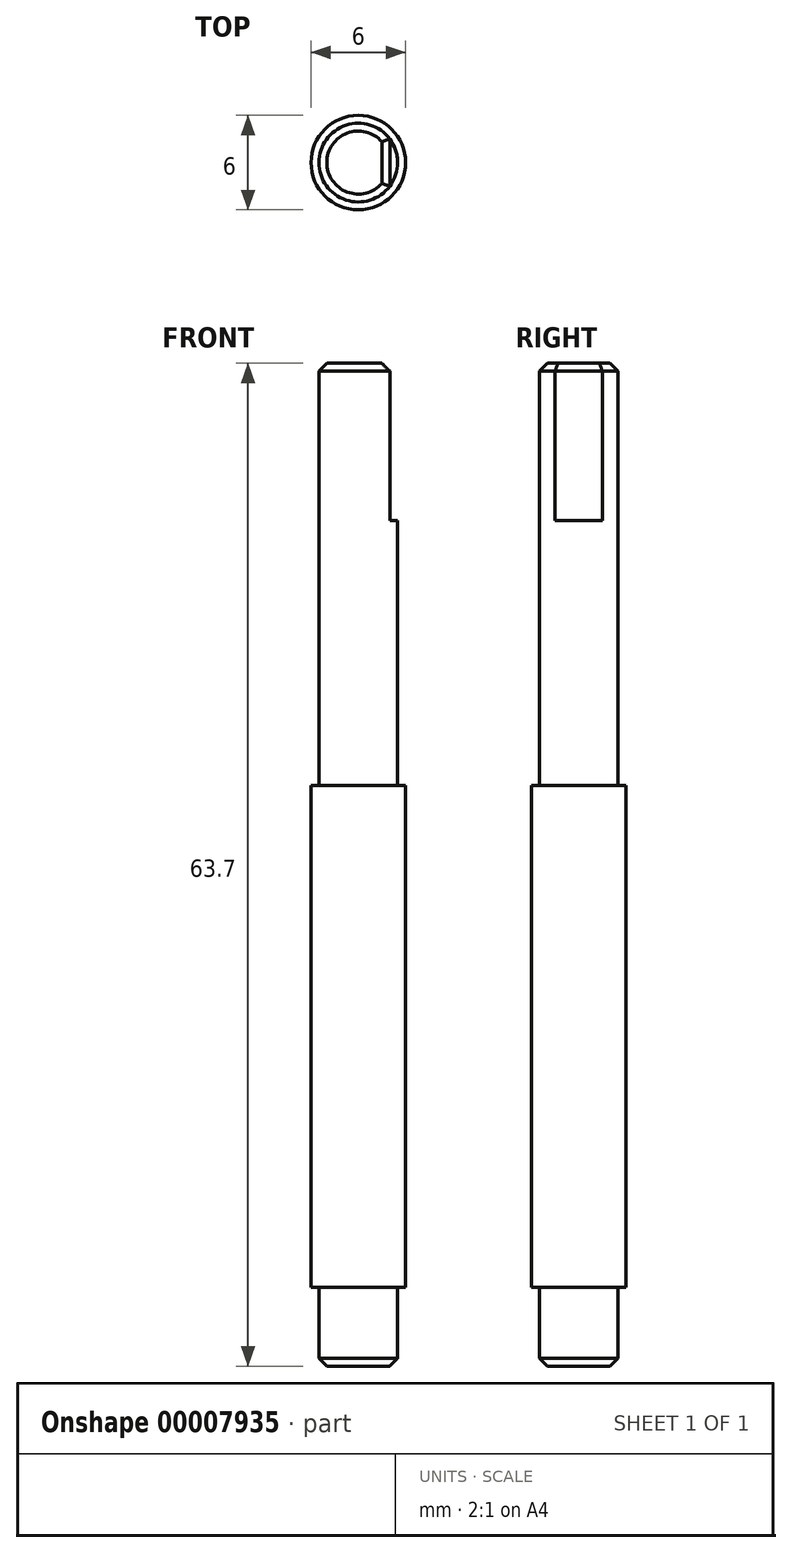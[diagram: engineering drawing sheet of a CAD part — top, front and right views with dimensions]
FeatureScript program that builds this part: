
annotation { "Feature Type Name" : "Feature", "Feature Type Description" : "" }
export const myFeature = defineFeature(function(context is Context, id is Id, definition is map)
    precondition{}
    {
        {
            var Q0;
            Q0=qCreatedBy(makeId("Top.planeOp"),FACE);
            var sketch = newSketch(context, id + "F0", { "sketchPlane" : qUnion([Q0])});
            skCircle(sketch, "E0", {"center": v(0, 0) * mm, "radius": 3 * mm});
            skCircle(sketch, "E1", {"center": v(0, 0) * mm, "radius": 2.5 * mm});
            skSolve(sketch);
        }
        {
            var Q0;
            Q0=makeQuery(id+"F0.imprint","IMPRINT",FACE,{"disambiguationData":[TD([[makeQuery(id+"F0.imprint","IMPRINT",EDGE,{"derivedFrom":sQuery(id+"F0.wireOp",EDGE,"E1")}),1.0]])]});
            extrude(context, id + "F1", {"entities" : qUnion([Q0]), "depth" : 42.2 * mm});
        }
        {
            var Q0;
            Q0=makeQuery(id+"F0.imprint","IMPRINT",FACE,{"disambiguationData":[TD([[makeQuery(id+"F0.imprint","IMPRINT",EDGE,{"derivedFrom":sQuery(id+"F0.wireOp",EDGE,"E0")}),1.0]])]});
            extrude(context, id + "F2", {"entities" : qUnion([Q0]), "operationType" : NewBodyOperationType.ADD, "depth" : 15.4 * mm});
        }
        {
            var Q0;
            Q0=makeQuery(id+"F0.imprint","IMPRINT",FACE,{"disambiguationData":[TD([[makeQuery(id+"F0.imprint","IMPRINT",EDGE,{"derivedFrom":sQuery(id+"F0.wireOp",EDGE,"E1")}),1.0]])]});
            extrude(context, id + "F3", {"entities" : qUnion([Q0]), "operationType" : NewBodyOperationType.ADD, "oppositeDirection" : true, "depth" : 21.5 * mm});
        }
        {
            var Q0;
            Q0=makeQuery(id+"F0.imprint","IMPRINT",FACE,{"disambiguationData":[TD([[makeQuery(id+"F0.imprint","IMPRINT",EDGE,{"derivedFrom":sQuery(id+"F0.wireOp",EDGE,"E0")}),1.0]])]});
            extrude(context, id + "F4", {"entities" : qUnion([Q0]), "operationType" : NewBodyOperationType.ADD, "oppositeDirection" : true, "depth" : 16.5 * mm});
        }
        {
            var Q0;
            Q0=makeQuery(id+"F3.opExtrude","CAP_FACE",FACE,{"disambiguationData":[OSD([sQuery(id+"F0.wireOp",EDGE,"E1")])],"isStart":false});
            chamfer(context, id + "F5", {"entities" : qUnion([Q0]), "width" : .5 * mm, "tangentPropagation" : true});
        }
        {
            var Q0;
            Q0=makeQuery(id+"F1.opExtrude","CAP_FACE",FACE,{"disambiguationData":[OSD([sQuery(id+"F0.wireOp",EDGE,"E1")])],"isStart":false});
            var sketch = newSketch(context, id + "F6", { "sketchPlane" : qUnion([Q0])});
            skLineSegment(sketch, "E2", {"start": v(2, 1.5) * mm, "end": v(2, -1.5) * mm});
            skLineSegment(sketch, "E3", {"start": v(2, 0) * mm, "end": v(-2.5, 0) * mm, "construction": true});
            skSolve(sketch);
        }
        {
            var Q0;
            {var subQ1=sQuery(id+"F6.wireOp",EDGE,"E2");Q0=makeQuery(id+"F6.imprint","IMPRINT",FACE,{"disambiguationData":[TD([[makeQuery(id+"F6.imprint","IMPRINT",EDGE,{"derivedFrom":subQ1}),1.0]])]});}
            extrude(context, id + "F7", {"entities" : qUnion([Q0]), "operationType" : NewBodyOperationType.REMOVE, "oppositeDirection" : true, "depth" : 10 * mm});
        }
        {
            var Q0;
            Q0=makeQuery(id+"F1.opExtrude","CAP_FACE",FACE,{"disambiguationData":[OSD([sQuery(id+"F0.wireOp",EDGE,"E1")])],"isStart":false});
            chamfer(context, id + "F8", {"entities" : qUnion([Q0]), "width" : .5 * mm, "tangentPropagation" : true});
        }
    });
